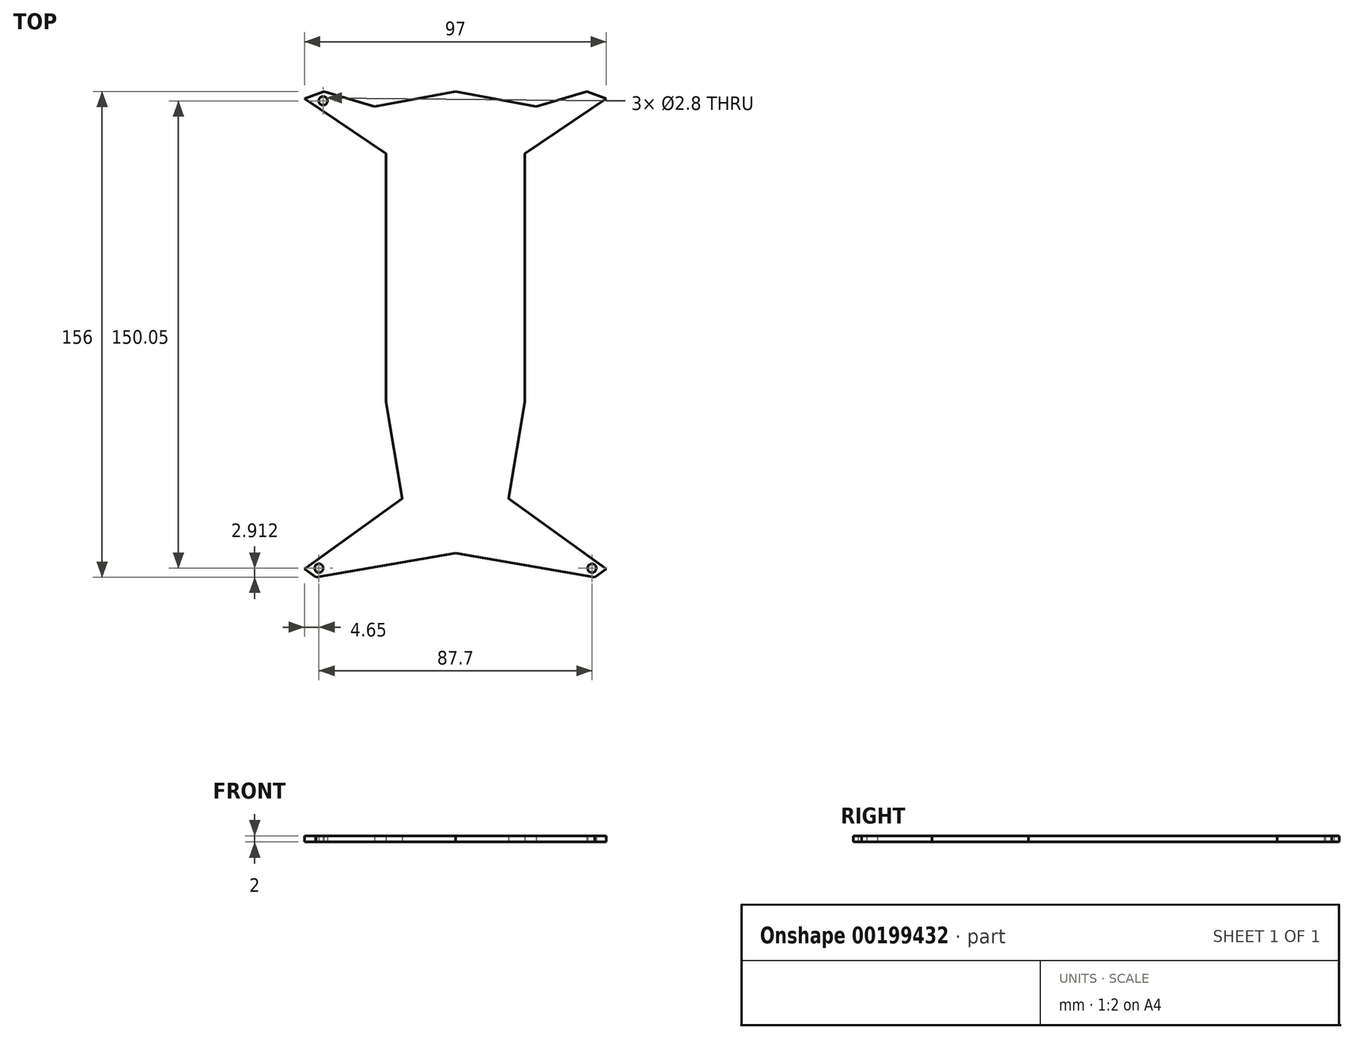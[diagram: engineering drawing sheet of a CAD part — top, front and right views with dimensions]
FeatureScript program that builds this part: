
annotation { "Feature Type Name" : "Feature", "Feature Type Description" : "" }
export const myFeature = defineFeature(function(context is Context, id is Id, definition is map)
    precondition{}
    {
        {
            var Q0;
            Q0=qCreatedBy(makeId("Top.planeOp"),FACE);
            var sketch = newSketch(context, id + "F0", { "sketchPlane" : qUnion([Q0])});
            skLineSegment(sketch, "E0.bottom", {"start": v(48.5, 78) * mm, "end": v(-48.5, 78) * mm, "construction": true});
            skLineSegment(sketch, "E0.top", {"start": v(48.5, -78) * mm, "end": v(-48.5, -78) * mm, "construction": true});
            skLineSegment(sketch, "E0.left", {"start": v(48.5, 78) * mm, "end": v(48.5, -78) * mm, "construction": true});
            skLineSegment(sketch, "E0.right", {"start": v(-48.5, 78) * mm, "end": v(-48.5, -78) * mm, "construction": true});
            skPoint(sketch, "E0.middle", {"position": v(0, 0) * mm});
            skLineSegment(sketch, "E1.bottom", {"start": v(9, -75.98) * mm, "end": v(-9, -75.98) * mm, "construction": true});
            skLineSegment(sketch, "E1.top", {"start": v(9, -3.98) * mm, "end": v(-9, -3.98) * mm, "construction": true});
            skLineSegment(sketch, "E1.left", {"start": v(9, -75.98) * mm, "end": v(9, -3.98) * mm, "construction": true});
            skLineSegment(sketch, "E1.right", {"start": v(-9, -75.98) * mm, "end": v(-9, -3.98) * mm, "construction": true});
            skPoint(sketch, "E1.middle", {"position": v(0, -39.98) * mm});
            skLineSegment(sketch, "E2.bottom", {"start": v(17, 67) * mm, "end": v(-17, 67) * mm, "construction": true});
            skLineSegment(sketch, "E2.top", {"start": v(17, -1) * mm, "end": v(-17, -1) * mm, "construction": true});
            skLineSegment(sketch, "E2.left", {"start": v(17, 67) * mm, "end": v(17, -1) * mm, "construction": true});
            skLineSegment(sketch, "E2.right", {"start": v(-17, 67) * mm, "end": v(-17, -1) * mm, "construction": true});
            skPoint(sketch, "E2.middle", {"position": v(0, 33) * mm});
            skLineSegment(sketch, "E3", {"start": v(0, -78) * mm, "end": v(0, 78) * mm, "construction": true});
            skLineSegment(sketch, "E4", {"start": v(0, 78) * mm, "end": v(-26, 73.16) * mm});
            skLineSegment(sketch, "E5", {"start": v(-26, 73.16) * mm, "end": v(-42.24, 78) * mm});
            skLineSegment(sketch, "E6", {"start": v(-42.24, 78) * mm, "end": v(-48.5, 75.67) * mm});
            skLineSegment(sketch, "E7", {"start": v(-48.5, 75.67) * mm, "end": v(-22.29, 58.04) * mm});
            skLineSegment(sketch, "E8", {"start": v(-22.29, 58.04) * mm, "end": v(-22.29, -21.74) * mm});
            skLineSegment(sketch, "E9", {"start": v(-22.29, -21.74) * mm, "end": v(-17.06, -52.74) * mm});
            skLineSegment(sketch, "E10", {"start": v(-17.06, -52.74) * mm, "end": v(-48.5, -75.38) * mm});
            skLineSegment(sketch, "E11", {"start": v(-48.5, -75.38) * mm, "end": v(-44.74, -78) * mm});
            skLineSegment(sketch, "E12", {"start": v(-44.74, -78) * mm, "end": v(0, -70.3) * mm});
            skCircle(sketch, "E13", {"center": v(-42.53, 74.96) * mm, "radius": 1.4 * mm});
            skCircle(sketch, "E14", {"center": v(-43.85, -75.09) * mm, "radius": 1.4 * mm});
            skLineSegment(sketch, "E15.MirrorCS", {"start": v(0, 78) * mm, "end": v(26, 73.16) * mm});
            skLineSegment(sketch, "E16.MirrorCS", {"start": v(26, 73.16) * mm, "end": v(42.24, 78) * mm});
            skLineSegment(sketch, "E17.MirrorCS", {"start": v(42.24, 78) * mm, "end": v(48.5, 75.67) * mm});
            skLineSegment(sketch, "E18.MirrorCS", {"start": v(48.5, 75.67) * mm, "end": v(22.29, 58.04) * mm});
            skLineSegment(sketch, "E19.MirrorCS", {"start": v(22.29, 58.04) * mm, "end": v(22.29, -21.74) * mm});
            skLineSegment(sketch, "E20.MirrorCS", {"start": v(22.29, -21.74) * mm, "end": v(17.06, -52.74) * mm});
            skLineSegment(sketch, "E21.MirrorCS", {"start": v(17.06, -52.74) * mm, "end": v(48.5, -75.38) * mm});
            skLineSegment(sketch, "E22.MirrorCS", {"start": v(48.5, -75.38) * mm, "end": v(44.74, -78) * mm});
            skLineSegment(sketch, "E23.MirrorCS", {"start": v(44.74, -78) * mm, "end": v(0, -70.3) * mm});
            skCircle(sketch, "E24.MirrorC", {"center": v(43.85, -75.09) * mm, "radius": 1.4 * mm});
            skSolve(sketch);
        }
        {
            var Q0;
            Q0 = qSketchRegion(id + "F0", true);
            extrude(context, id + "F1", {"entities" : qUnion([Q0]), "depth" : 2 * mm});
        }
    });
